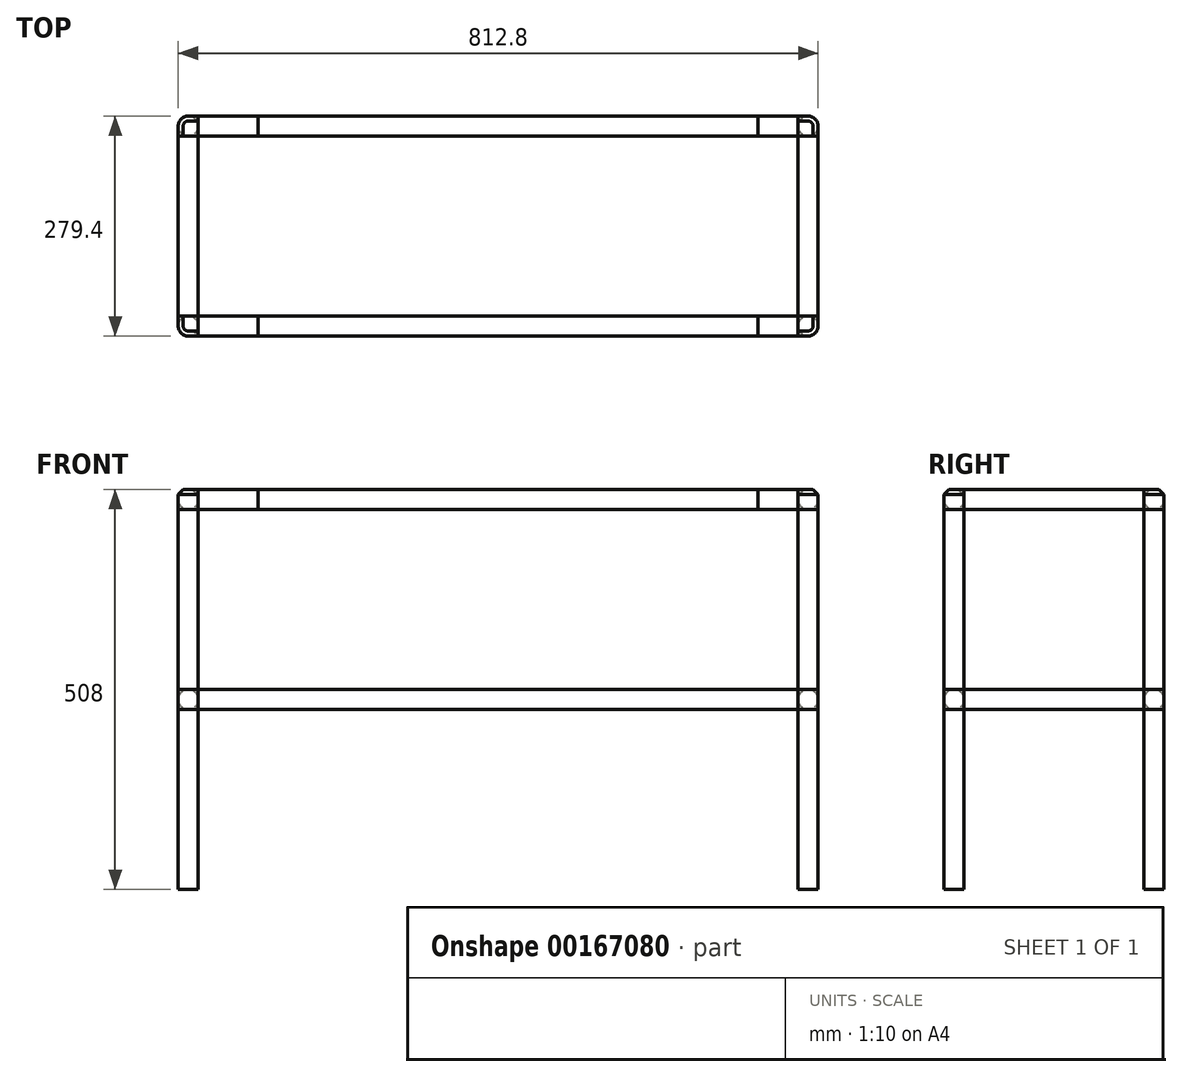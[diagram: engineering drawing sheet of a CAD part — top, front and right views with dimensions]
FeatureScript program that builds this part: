
annotation { "Feature Type Name" : "Feature", "Feature Type Description" : "" }
export const myFeature = defineFeature(function(context is Context, id is Id, definition is map)
    precondition{}
    {
        {
            var Q0;
            Q0=qCreatedBy(makeId("Right.planeOp"),FACE);
            cPlane(context, id + "F0", {"entities" : qUnion([Q0]), "cplaneType" : CPlaneType.OFFSET, "offset" : 393.7 * mm, "width" : 152.4 * mm, "height" : 152.4 * mm});
        }
        {
            var Q0;
            Q0=qCreatedBy(makeId("Front.planeOp"),FACE);
            cPlane(context, id + "F1", {"entities" : qUnion([Q0]), "cplaneType" : CPlaneType.OFFSET, "offset" : 127 * mm, "width" : 152.4 * mm, "height" : 152.4 * mm});
        }
        {
            var Q0;
            Q0=qCreatedBy(makeId("Top.planeOp"),FACE);
            cPlane(context, id + "F2", {"entities" : qUnion([Q0]), "cplaneType" : CPlaneType.OFFSET, "offset" : 762 * mm, "width" : 152.4 * mm, "height" : 152.4 * mm});
        }
        {
            var Q0;
            Q0=qCreatedBy(id+"F2.planeOp",FACE);
            cPlane(context, id + "F3", {"entities" : qUnion([Q0]), "cplaneType" : CPlaneType.OFFSET, "offset" : 228.6 * mm, "oppositeDirection" : true, "width" : 152.4 * mm, "height" : 152.4 * mm});
        }
        {
            var Q0;
            Q0=qCreatedBy(id+"F3.planeOp",FACE);
            var sketch = newSketch(context, id + "F4", { "sketchPlane" : qUnion([Q0])});
            skLineSegment(sketch, "E0.bottom", {"start": v(12.7, -12.7) * mm, "end": v(-12.7, -12.7) * mm});
            skLineSegment(sketch, "E0.top", {"start": v(12.7, 12.7) * mm, "end": v(-12.7, 12.7) * mm});
            skLineSegment(sketch, "E0.left", {"start": v(12.7, -12.7) * mm, "end": v(12.7, 12.7) * mm});
            skLineSegment(sketch, "E0.right", {"start": v(-12.7, -12.7) * mm, "end": v(-12.7, 12.7) * mm});
            skPoint(sketch, "E0.middle", {"position": v(0, 0) * mm});
            skLineSegment(sketch, "E1.bottom", {"start": v(-12.7, -266.7) * mm, "end": v(12.7, -266.7) * mm});
            skLineSegment(sketch, "E1.top", {"start": v(-12.7, -241.3) * mm, "end": v(12.7, -241.3) * mm});
            skLineSegment(sketch, "E1.left", {"start": v(-12.7, -266.7) * mm, "end": v(-12.7, -241.3) * mm});
            skLineSegment(sketch, "E1.right", {"start": v(12.7, -266.7) * mm, "end": v(12.7, -241.3) * mm});
            skPoint(sketch, "E1.middle", {"position": v(0, -254) * mm});
            skLineSegment(sketch, "E2.bottom", {"start": v(800.1, -266.7) * mm, "end": v(774.7, -266.7) * mm});
            skLineSegment(sketch, "E2.top", {"start": v(800.1, -241.3) * mm, "end": v(774.7, -241.3) * mm});
            skLineSegment(sketch, "E2.left", {"start": v(800.1, -266.7) * mm, "end": v(800.1, -241.3) * mm});
            skLineSegment(sketch, "E2.right", {"start": v(774.7, -266.7) * mm, "end": v(774.7, -241.3) * mm});
            skPoint(sketch, "E2.middle", {"position": v(787.4, -254) * mm});
            skLineSegment(sketch, "E3.bottom", {"start": v(800.1, 12.7) * mm, "end": v(774.7, 12.7) * mm});
            skLineSegment(sketch, "E3.top", {"start": v(800.1, -12.7) * mm, "end": v(774.7, -12.7) * mm});
            skLineSegment(sketch, "E3.left", {"start": v(800.1, 12.7) * mm, "end": v(800.1, -12.7) * mm});
            skLineSegment(sketch, "E3.right", {"start": v(774.7, 12.7) * mm, "end": v(774.7, -12.7) * mm});
            skPoint(sketch, "E3.middle", {"position": v(787.4, 0) * mm});
            skLineSegment(sketch, "E4", {"start": v(0, 0) * mm, "end": v(787.4, 0) * mm});
            skLineSegment(sketch, "E5", {"start": v(787.4, 0) * mm, "end": v(787.4, -254) * mm});
            skSolve(sketch);
        }
        {
            var Q0;
            Q0 = qSketchRegion(id + "F4", true);
            extrude(context, id + "F5", {"entities" : qUnion([Q0]), "oppositeDirection" : true, "depth" : 25.4 * mm});
        }
        {
            var Q0;
            Q0=makeQuery(id+"F5.opExtrude","SWEPT_EDGE",EDGE,{"disambiguationData":[OSD([sQuery(id+"F4.wireOp",EDGE,"E0.top"),sQuery(id+"F4.wireOp",EDGE,"E0.right")])]});
            var Q1;
            Q1=makeQuery(id+"F5.opExtrude","SWEPT_EDGE",EDGE,{"disambiguationData":[OSD([sQuery(id+"F4.wireOp",EDGE,"E1.bottom"),sQuery(id+"F4.wireOp",EDGE,"E1.left")])]});
            var Q2;
            Q2=makeQuery(id+"F5.opExtrude","SWEPT_EDGE",EDGE,{"disambiguationData":[OSD([sQuery(id+"F4.wireOp",EDGE,"E2.bottom"),sQuery(id+"F4.wireOp",EDGE,"E2.left")])]});
            var Q3;
            Q3=makeQuery(id+"F5.opExtrude","SWEPT_EDGE",EDGE,{"disambiguationData":[OSD([sQuery(id+"F4.wireOp",EDGE,"E3.bottom"),sQuery(id+"F4.wireOp",EDGE,"E3.left")])]});
            fillet(context, id + "F6", {"entities" : qUnion([Q0, Q1, Q2, Q3]), "radius" : 12.7 * mm, "tangentPropagation" : true, "allowEdgeOverflow" : false});
        }
        {
            var Q0;
            Q0=makeQuery(id+"F5.opExtrude","SWEPT_FACE",FACE,{"disambiguationData":[OSD([sQuery(id+"F4.wireOp",EDGE,"E1.right")])]});
            cPlane(context, id + "F7", {"entities" : qUnion([Q0]), "cplaneType" : CPlaneType.OFFSET, "offset" : 393.7 * mm, "width" : 152.4 * mm, "height" : 152.4 * mm});
        }
        {
            var Q0;
            Q0=qCreatedBy(id+"F7.planeOp",FACE);
            var sketch = newSketch(context, id + "F8", { "sketchPlane" : qUnion([Q0])});
            skCircle(sketch, "E6", {"center": v(-254, 520.7) * mm, "radius": 12.7 * mm});
            skCircle(sketch, "E7", {"center": v(0, 520.7) * mm, "radius": 12.7 * mm});
            skSolve(sketch);
        }
        {
            var Q0;
            Q0=makeQuery(id+"F5.opExtrude","SWEPT_FACE",FACE,{"disambiguationData":[OSD([sQuery(id+"F4.wireOp",EDGE,"E1.top")])]});
            cPlane(context, id + "F9", {"entities" : qUnion([Q0]), "cplaneType" : CPlaneType.OFFSET, "offset" : 114.3 * mm, "width" : 152.4 * mm, "height" : 152.4 * mm});
        }
        {
            var Q0;
            Q0=qCreatedBy(id+"F9.planeOp",FACE);
            var sketch = newSketch(context, id + "F10", { "sketchPlane" : qUnion([Q0])});
            skLineSegment(sketch, "E8", {"start": v(0, 0) * mm, "end": v(0, 520.7) * mm});
            skLineSegment(sketch, "E9", {"start": v(0, 520.7) * mm, "end": v(-787.4, 520.7) * mm});
            skCircle(sketch, "E10", {"center": v(-787.4, 520.7) * mm, "radius": 12.7 * mm});
            skCircle(sketch, "E11", {"center": v(0, 520.7) * mm, "radius": 12.7 * mm});
            skSolve(sketch);
        }
        {
            var Q0;
            Q0 = qSketchRegion(id + "F10", true);
            extrude(context, id + "F11", {"entities" : qUnion([Q0]), "endBound" : BoundingType.SYMMETRIC, "depth" : 228.6 * mm});
        }
        {
            var Q0;
            Q0=qCreatedBy(id+"F3.planeOp",FACE);
            cPlane(context, id + "F12", {"entities" : qUnion([Q0]), "cplaneType" : CPlaneType.OFFSET, "offset" : 25.4 * mm, "oppositeDirection" : true, "width" : 152.4 * mm, "height" : 152.4 * mm});
        }
        {
            var Q0;
            Q0=qCreatedBy(id+"F12.planeOp",FACE);
            var sketch = newSketch(context, id + "F13", { "sketchPlane" : qUnion([Q0])});
            skLineSegment(sketch, "E12", {"start": v(0, 0) * mm, "end": v(0, -254) * mm});
            skLineSegment(sketch, "E13", {"start": v(0, -254) * mm, "end": v(787.4, -254) * mm});
            skLineSegment(sketch, "E14", {"start": v(787.4, -254) * mm, "end": v(787.4, 0) * mm});
            skCircle(sketch, "E15", {"center": v(0, 0) * mm, "radius": 12.7 * mm});
            skCircle(sketch, "E16", {"center": v(0, -254) * mm, "radius": 12.7 * mm});
            skCircle(sketch, "E17", {"center": v(787.4, -254) * mm, "radius": 12.7 * mm});
            skCircle(sketch, "E18", {"center": v(787.4, 0) * mm, "radius": 12.7 * mm});
            skSolve(sketch);
        }
        {
            var Q0;
            Q0 = qSketchRegion(id + "F13", true);
            extrude(context, id + "F14", {"entities" : qUnion([Q0]), "oppositeDirection" : true, "depth" : 228.6 * mm});
        }
        {
            var Q0;
            Q0=qCreatedBy(id+"F12.planeOp",FACE);
            cPlane(context, id + "F15", {"entities" : qUnion([Q0]), "cplaneType" : CPlaneType.OFFSET, "offset" : 228.6 * mm, "oppositeDirection" : true, "width" : 152.4 * mm, "height" : 152.4 * mm});
        }
        {
            var Q0;
            Q0=qCreatedBy(id+"F15.planeOp",FACE);
            var sketch = newSketch(context, id + "F16", { "sketchPlane" : qUnion([Q0])});
            skLineSegment(sketch, "E19.bottom", {"start": v(12.7, -12.7) * mm, "end": v(-12.7, -12.7) * mm});
            skLineSegment(sketch, "E19.top", {"start": v(12.7, 12.7) * mm, "end": v(-12.7, 12.7) * mm});
            skLineSegment(sketch, "E19.left", {"start": v(12.7, -12.7) * mm, "end": v(12.7, 12.7) * mm});
            skLineSegment(sketch, "E19.right", {"start": v(-12.7, -12.7) * mm, "end": v(-12.7, 12.7) * mm});
            skPoint(sketch, "E19.middle", {"position": v(0, 0) * mm});
            skLineSegment(sketch, "E20.bottom", {"start": v(-12.7, -266.7) * mm, "end": v(12.7, -266.7) * mm});
            skLineSegment(sketch, "E20.top", {"start": v(-12.7, -241.3) * mm, "end": v(12.7, -241.3) * mm});
            skLineSegment(sketch, "E20.left", {"start": v(-12.7, -266.7) * mm, "end": v(-12.7, -241.3) * mm});
            skLineSegment(sketch, "E20.right", {"start": v(12.7, -266.7) * mm, "end": v(12.7, -241.3) * mm});
            skPoint(sketch, "E20.middle", {"position": v(0, -254) * mm});
            skLineSegment(sketch, "E21.bottom", {"start": v(800.1, -266.7) * mm, "end": v(774.7, -266.7) * mm});
            skLineSegment(sketch, "E21.top", {"start": v(800.1, -241.3) * mm, "end": v(774.7, -241.3) * mm});
            skLineSegment(sketch, "E21.left", {"start": v(800.1, -266.7) * mm, "end": v(800.1, -241.3) * mm});
            skLineSegment(sketch, "E21.right", {"start": v(774.7, -266.7) * mm, "end": v(774.7, -241.3) * mm});
            skPoint(sketch, "E21.middle", {"position": v(787.4, -254) * mm});
            skLineSegment(sketch, "E22.bottom", {"start": v(800.1, 12.7) * mm, "end": v(774.7, 12.7) * mm});
            skLineSegment(sketch, "E22.top", {"start": v(800.1, -12.7) * mm, "end": v(774.7, -12.7) * mm});
            skLineSegment(sketch, "E22.left", {"start": v(800.1, 12.7) * mm, "end": v(800.1, -12.7) * mm});
            skLineSegment(sketch, "E22.right", {"start": v(774.7, 12.7) * mm, "end": v(774.7, -12.7) * mm});
            skPoint(sketch, "E22.middle", {"position": v(787.4, 0) * mm});
            skLineSegment(sketch, "E23", {"start": v(0, 0) * mm, "end": v(787.4, 0) * mm});
            skLineSegment(sketch, "E24", {"start": v(787.4, 0) * mm, "end": v(787.4, -254) * mm});
            skSolve(sketch);
        }
        {
            var Q0;
            Q0 = qSketchRegion(id + "F16", true);
            extrude(context, id + "F17", {"entities" : qUnion([Q0]), "oppositeDirection" : true, "depth" : 25.4 * mm});
        }
        {
            var Q0;
            Q0=makeQuery(id+"F17.opExtrude","SWEPT_EDGE",EDGE,{"disambiguationData":[OSD([sQuery(id+"F16.wireOp",EDGE,"E20.bottom"),sQuery(id+"F16.wireOp",EDGE,"E20.left")])]});
            var Q1;
            Q1=makeQuery(id+"F17.opExtrude","SWEPT_EDGE",EDGE,{"disambiguationData":[OSD([sQuery(id+"F16.wireOp",EDGE,"E19.top"),sQuery(id+"F16.wireOp",EDGE,"E19.right")])]});
            var Q2;
            Q2=makeQuery(id+"F17.opExtrude","SWEPT_EDGE",EDGE,{"disambiguationData":[OSD([sQuery(id+"F16.wireOp",EDGE,"E21.bottom"),sQuery(id+"F16.wireOp",EDGE,"E21.left")])]});
            var Q3;
            Q3=makeQuery(id+"F17.opExtrude","SWEPT_EDGE",EDGE,{"disambiguationData":[OSD([sQuery(id+"F16.wireOp",EDGE,"E22.bottom"),sQuery(id+"F16.wireOp",EDGE,"E22.left")])]});
            fillet(context, id + "F18", {"entities" : qUnion([Q0, Q1, Q2, Q3]), "radius" : 12.7 * mm, "tangentPropagation" : true, "allowEdgeOverflow" : false});
        }
        {
            var Q0;
            Q0=makeQuery(id+"F17.opExtrude","SWEPT_FACE",FACE,{"disambiguationData":[OSD([sQuery(id+"F16.wireOp",EDGE,"E20.right")])]});
            cPlane(context, id + "F19", {"entities" : qUnion([Q0]), "cplaneType" : CPlaneType.OFFSET, "offset" : 381 * mm, "width" : 152.4 * mm, "height" : 152.4 * mm});
        }
        {
            var Q0;
            Q0=makeQuery(id+"F17.opExtrude","SWEPT_FACE",FACE,{"disambiguationData":[OSD([sQuery(id+"F16.wireOp",EDGE,"E22.top")])]});
            cPlane(context, id + "F20", {"entities" : qUnion([Q0]), "cplaneType" : CPlaneType.OFFSET, "offset" : 114.3 * mm, "width" : 152.4 * mm, "height" : 152.4 * mm});
        }
        {
            var Q0;
            Q0=qCreatedBy(id+"F19.planeOp",FACE);
            var sketch = newSketch(context, id + "F21", { "sketchPlane" : qUnion([Q0])});
            skLineSegment(sketch, "E25", {"start": v(0, 0) * mm, "end": v(0, 266.7) * mm});
            skLineSegment(sketch, "E26", {"start": v(0, 266.7) * mm, "end": v(-254, 266.7) * mm});
            skCircle(sketch, "E27", {"center": v(-254, 266.7) * mm, "radius": 12.7 * mm});
            skCircle(sketch, "E28", {"center": v(0, 266.7) * mm, "radius": 12.7 * mm});
            skSolve(sketch);
        }
        {
            var Q0;
            Q0 = qSketchRegion(id + "F21", true);
            extrude(context, id + "F22", {"entities" : qUnion([Q0]), "endBound" : BoundingType.SYMMETRIC, "depth" : 762 * mm});
        }
        {
            var Q0;
            Q0=qCreatedBy(id+"F20.planeOp",FACE);
            var sketch = newSketch(context, id + "F23", { "sketchPlane" : qUnion([Q0])});
            skLineSegment(sketch, "E29", {"start": v(0, 0) * mm, "end": v(0, 266.7) * mm});
            skLineSegment(sketch, "E30", {"start": v(0, 266.7) * mm, "end": v(787.4, 266.7) * mm});
            skCircle(sketch, "E31", {"center": v(787.4, 266.7) * mm, "radius": 12.7 * mm});
            skCircle(sketch, "E32", {"center": v(0, 266.7) * mm, "radius": 12.7 * mm});
            skSolve(sketch);
        }
        {
            var Q0;
            Q0 = qSketchRegion(id + "F23", true);
            extrude(context, id + "F24", {"entities" : qUnion([Q0]), "endBound" : BoundingType.SYMMETRIC, "depth" : 228.6 * mm});
        }
        {
            var Q0;
            Q0=qCreatedBy(id+"F15.planeOp",FACE);
            cPlane(context, id + "F25", {"entities" : qUnion([Q0]), "cplaneType" : CPlaneType.OFFSET, "offset" : 25.4 * mm, "oppositeDirection" : true, "width" : 152.4 * mm, "height" : 152.4 * mm});
        }
        {
            var Q0;
            Q0=qCreatedBy(id+"F25.planeOp",FACE);
            var sketch = newSketch(context, id + "F26", { "sketchPlane" : qUnion([Q0])});
            skLineSegment(sketch, "E33", {"start": v(0, 0) * mm, "end": v(0, -254) * mm});
            skLineSegment(sketch, "E34", {"start": v(0, -254) * mm, "end": v(787.4, -254) * mm});
            skLineSegment(sketch, "E35", {"start": v(787.4, -254) * mm, "end": v(787.4, 0) * mm});
            skCircle(sketch, "E36", {"center": v(0, 0) * mm, "radius": 12.7 * mm});
            skCircle(sketch, "E37", {"center": v(0, -254) * mm, "radius": 12.7 * mm});
            skCircle(sketch, "E38", {"center": v(787.4, -254) * mm, "radius": 12.7 * mm});
            skCircle(sketch, "E39", {"center": v(787.4, 0) * mm, "radius": 12.7 * mm});
            skSolve(sketch);
        }
        {
            var Q0;
            Q0 = qSketchRegion(id + "F26", true);
            extrude(context, id + "F27", {"entities" : qUnion([Q0]), "oppositeDirection" : true, "depth" : 228.6 * mm});
        }
        {
            var Q0;
            Q0 = qSketchRegion(id + "F8", true);
            extrude(context, id + "F28", {"entities" : qUnion([Q0]), "operationType" : NewBodyOperationType.ADD, "endBound" : BoundingType.SYMMETRIC, "depth" : 635 * mm});
        }
        {
            var Q0;
            Q0=qCreatedBy(id+"F0.planeOp",FACE);
            var sketch = newSketch(context, id + "F29", { "sketchPlane" : qUnion([Q0])});
            skLineSegment(sketch, "E40", {"start": v(0, 0) * mm, "end": v(0, 520.7) * mm});
            skLineSegment(sketch, "E41", {"start": v(0, 520.7) * mm, "end": v(-254, 520.7) * mm});
            skCircle(sketch, "E42", {"center": v(-254, 520.7) * mm, "radius": 12.7 * mm});
            skCircle(sketch, "E43", {"center": v(0, 520.7) * mm, "radius": 12.7 * mm});
            skSolve(sketch);
        }
        {
            var Q0;
            Q0 = qSketchRegion(id + "F29", true);
            extrude(context, id + "F30", {"entities" : qUnion([Q0]), "endBound" : BoundingType.SYMMETRIC, "depth" : 762 * mm});
        }
        {
            var Q0;
            Q0=makeQuery(id+"F5.opExtrude","CAP_EDGE",EDGE,{"disambiguationData":[OSD([sQuery(id+"F4.wireOp",EDGE,"E1.bottom")])],"isStart":true});
            var Q1;
            {var subQ0=sQuery(id+"F4.wireOp",EDGE,"E1.left");var subQ1=sQuery(id+"F4.wireOp",EDGE,"E1.bottom");Q1=makeQuery(id+"F6.opFillet","BLEND_EDGE",EDGE,{"blendedFrom":[makeQuery(id+"F5.opExtrude","SWEPT_EDGE",EDGE,{"disambiguationData":[OSD([subQ1,subQ0])]}),makeQuery(id+"F5.opExtrude","CAP_FACE",FACE,{"disambiguationData":[OSD([subQ1,sQuery(id+"F4.wireOp",EDGE,"E1.top"),subQ0,sQuery(id+"F4.wireOp",EDGE,"E1.right")])],"isStart":true})],"blendedInto":[makeQuery(id+"F5.opExtrude","CAP_FACE",FACE,{"disambiguationData":[OSD([subQ1,sQuery(id+"F4.wireOp",EDGE,"E1.top"),subQ0,sQuery(id+"F4.wireOp",EDGE,"E1.right")])],"isStart":true})]});}
            var Q2;
            Q2=makeQuery(id+"F5.opExtrude","CAP_EDGE",EDGE,{"disambiguationData":[OSD([sQuery(id+"F4.wireOp",EDGE,"E1.left")])],"isStart":true});
            var Q3;
            {var subQ0=sQuery(id+"F4.wireOp",EDGE,"E0.right");var subQ1=sQuery(id+"F4.wireOp",EDGE,"E0.top");Q3=makeQuery(id+"F6.opFillet","BLEND_EDGE",EDGE,{"blendedFrom":[makeQuery(id+"F5.opExtrude","SWEPT_EDGE",EDGE,{"disambiguationData":[OSD([subQ1,subQ0])]}),makeQuery(id+"F5.opExtrude","CAP_FACE",FACE,{"disambiguationData":[OSD([sQuery(id+"F4.wireOp",EDGE,"E0.bottom"),subQ1,sQuery(id+"F4.wireOp",EDGE,"E0.left"),subQ0])],"isStart":true})],"blendedInto":[makeQuery(id+"F5.opExtrude","CAP_FACE",FACE,{"disambiguationData":[OSD([sQuery(id+"F4.wireOp",EDGE,"E0.bottom"),subQ1,sQuery(id+"F4.wireOp",EDGE,"E0.left"),subQ0])],"isStart":true})]});}
            var Q4;
            Q4=makeQuery(id+"F5.opExtrude","CAP_EDGE",EDGE,{"disambiguationData":[OSD([sQuery(id+"F4.wireOp",EDGE,"E0.top")])],"isStart":true});
            var Q5;
            Q5=makeQuery(id+"F5.opExtrude","CAP_EDGE",EDGE,{"disambiguationData":[OSD([sQuery(id+"F4.wireOp",EDGE,"E0.right")])],"isStart":true});
            var Q6;
            Q6=makeQuery(id+"F5.opExtrude","CAP_EDGE",EDGE,{"disambiguationData":[OSD([sQuery(id+"F4.wireOp",EDGE,"E3.left")])],"isStart":true});
            var Q7;
            {var subQ0=sQuery(id+"F4.wireOp",EDGE,"E3.left");var subQ1=sQuery(id+"F4.wireOp",EDGE,"E3.bottom");Q7=makeQuery(id+"F6.opFillet","BLEND_EDGE",EDGE,{"blendedFrom":[makeQuery(id+"F5.opExtrude","SWEPT_EDGE",EDGE,{"disambiguationData":[OSD([subQ1,subQ0])]}),makeQuery(id+"F5.opExtrude","CAP_FACE",FACE,{"disambiguationData":[OSD([subQ1,sQuery(id+"F4.wireOp",EDGE,"E3.top"),subQ0,sQuery(id+"F4.wireOp",EDGE,"E3.right")])],"isStart":true})],"blendedInto":[makeQuery(id+"F5.opExtrude","CAP_FACE",FACE,{"disambiguationData":[OSD([subQ1,sQuery(id+"F4.wireOp",EDGE,"E3.top"),subQ0,sQuery(id+"F4.wireOp",EDGE,"E3.right")])],"isStart":true})]});}
            var Q8;
            Q8=makeQuery(id+"F5.opExtrude","CAP_EDGE",EDGE,{"disambiguationData":[OSD([sQuery(id+"F4.wireOp",EDGE,"E3.bottom")])],"isStart":true});
            var Q9;
            Q9=makeQuery(id+"F5.opExtrude","CAP_EDGE",EDGE,{"disambiguationData":[OSD([sQuery(id+"F4.wireOp",EDGE,"E2.bottom")])],"isStart":true});
            var Q10;
            {var subQ0=sQuery(id+"F4.wireOp",EDGE,"E2.left");var subQ1=sQuery(id+"F4.wireOp",EDGE,"E2.bottom");Q10=makeQuery(id+"F6.opFillet","BLEND_EDGE",EDGE,{"blendedFrom":[makeQuery(id+"F5.opExtrude","SWEPT_EDGE",EDGE,{"disambiguationData":[OSD([subQ1,subQ0])]}),makeQuery(id+"F5.opExtrude","CAP_FACE",FACE,{"disambiguationData":[OSD([subQ1,sQuery(id+"F4.wireOp",EDGE,"E2.top"),subQ0,sQuery(id+"F4.wireOp",EDGE,"E2.right")])],"isStart":true})],"blendedInto":[makeQuery(id+"F5.opExtrude","CAP_FACE",FACE,{"disambiguationData":[OSD([subQ1,sQuery(id+"F4.wireOp",EDGE,"E2.top"),subQ0,sQuery(id+"F4.wireOp",EDGE,"E2.right")])],"isStart":true})]});}
            var Q11;
            Q11=makeQuery(id+"F5.opExtrude","CAP_EDGE",EDGE,{"disambiguationData":[OSD([sQuery(id+"F4.wireOp",EDGE,"E2.left")])],"isStart":true});
            chamfer(context, id + "F31", {"entities" : qUnion([Q0, Q1, Q2, Q3, Q4, Q5, Q6, Q7, Q8, Q9, Q10, Q11]), "width" : 6.35 * mm, "tangentPropagation" : true});
        }
    });
